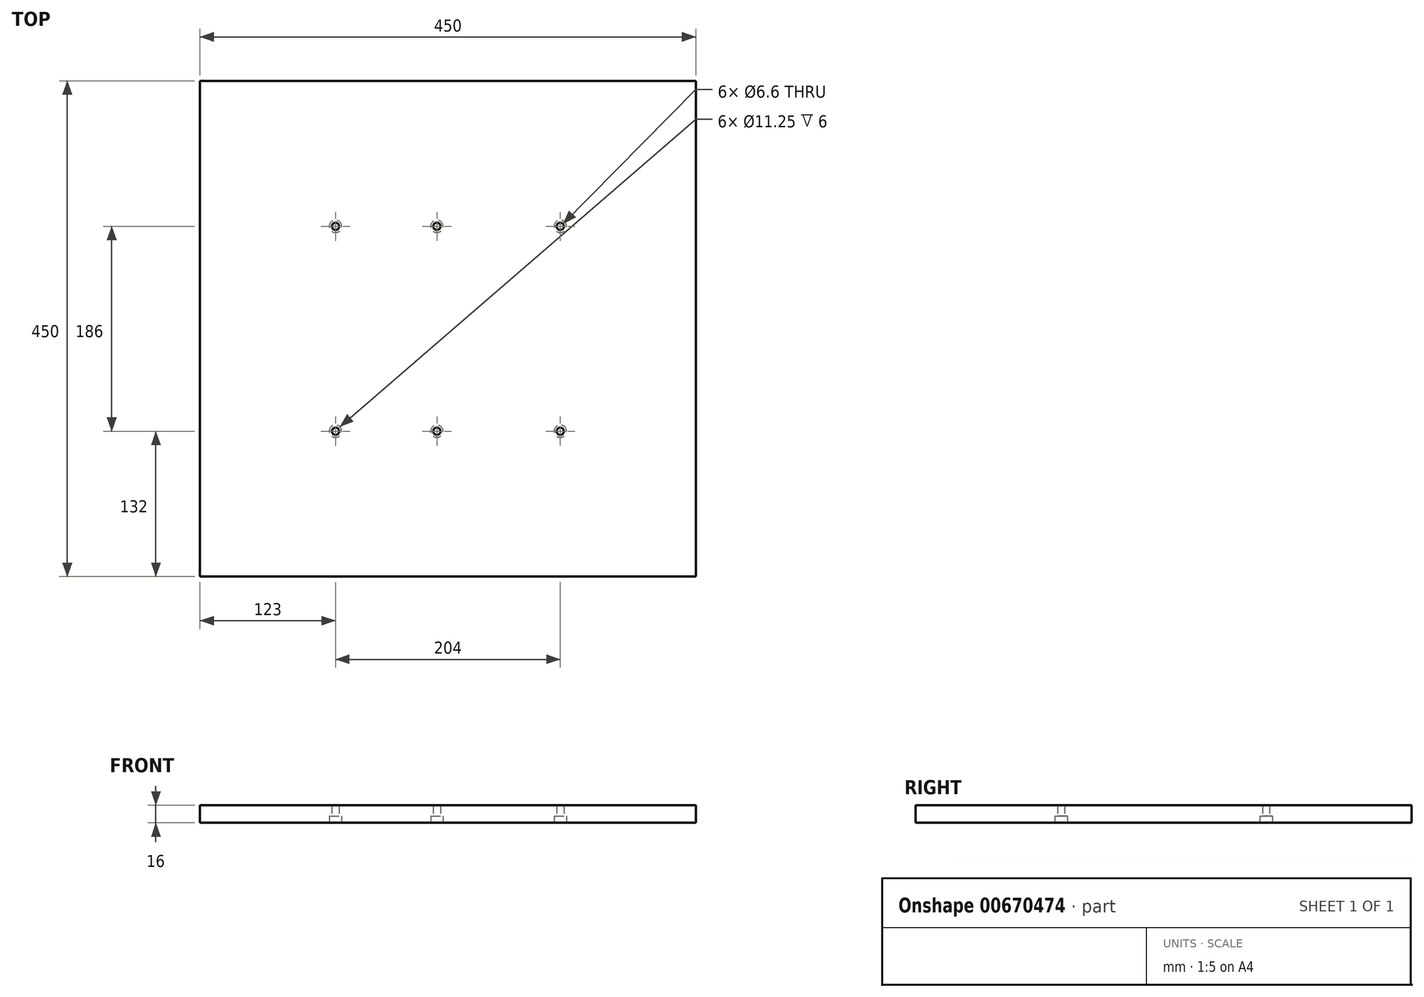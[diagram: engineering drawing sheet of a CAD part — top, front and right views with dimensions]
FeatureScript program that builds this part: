
annotation { "Feature Type Name" : "Feature", "Feature Type Description" : "" }
export const myFeature = defineFeature(function(context is Context, id is Id, definition is map)
    precondition{}
    {
        {
            var Q0;
            Q0=qCreatedBy(makeId("Top.planeOp"),FACE);
            var sketch = newSketch(context, id + "F0", { "sketchPlane" : qUnion([Q0])});
            skLineSegment(sketch, "E0.bottom", {"start": v(225, -225) * mm, "end": v(-225, -225) * mm});
            skLineSegment(sketch, "E0.top", {"start": v(225, 225) * mm, "end": v(-225, 225) * mm});
            skLineSegment(sketch, "E0.left", {"start": v(225, -225) * mm, "end": v(225, 225) * mm});
            skLineSegment(sketch, "E0.right", {"start": v(-225, -225) * mm, "end": v(-225, 225) * mm});
            skPoint(sketch, "E0.middle", {"position": v(0, 0) * mm});
            skSolve(sketch);
        }
        {
            var Q0;
            Q0 = qSketchRegion(id + "F0", true);
            extrude(context, id + "F1", {"entities" : qUnion([Q0]), "depth" : 16 * mm, "offsetDistance" : 25.4 * mm});
        }
        {
            var Q0;
            Q0=qCreatedBy(makeId("Top.planeOp"),FACE);
            var sketch = newSketch(context, id + "F2", { "sketchPlane" : qUnion([Q0])});
            skCircle(sketch, "E1", {"center": v(-102, -93) * mm, "radius": 3.3 * mm});
            skCircle(sketch, "E2", {"center": v(-10, -93) * mm, "radius": 3.3 * mm});
            skCircle(sketch, "E3", {"center": v(102, -93) * mm, "radius": 3.3 * mm});
            skCircle(sketch, "E4", {"center": v(-10, 93) * mm, "radius": 3.3 * mm});
            skCircle(sketch, "E5", {"center": v(102, 93) * mm, "radius": 3.3 * mm});
            skCircle(sketch, "E6", {"center": v(-102, 93) * mm, "radius": 3.3 * mm});
            skLineSegment(sketch, "E7.bottom", {"start": v(-102, 93) * mm, "end": v(102, 93) * mm, "construction": true});
            skLineSegment(sketch, "E7.top", {"start": v(-102, -93) * mm, "end": v(102, -93) * mm, "construction": true});
            skLineSegment(sketch, "E7.left", {"start": v(-102, 93) * mm, "end": v(-102, -93) * mm, "construction": true});
            skLineSegment(sketch, "E7.right", {"start": v(102, 93) * mm, "end": v(102, -93) * mm, "construction": true});
            skLineSegment(sketch, "E8", {"start": v(-102, -93) * mm, "end": v(102, 93) * mm, "construction": true});
            skLineSegment(sketch, "E9", {"start": v(-102, 93) * mm, "end": v(102, -93) * mm, "construction": true});
            skPoint(sketch, "E10", {"position": v(0, 0) * mm});
            skSolve(sketch);
        }
        {
            var Q0;
            Q0=sQuery(id+"F2.wireOp",VERTEX,"E7.left.start");
            var Q1;
            Q1=sQuery(id+"F2.wireOp",VERTEX,"E7.left.end");
            var Q2;
            Q2=sQuery(id+"F2.wireOp",VERTEX,"E2.center");
            var Q3;
            Q3=sQuery(id+"F2.wireOp",VERTEX,"E4.center");
            var Q4;
            Q4=sQuery(id+"F2.wireOp",VERTEX,"E7.right.start");
            var Q5;
            Q5=sQuery(id+"F2.wireOp",VERTEX,"E7.top.end");
            var Q6;
            Q6=makeQuery(id+"F1.opExtrude","SWEPT_BODY",BODY,{"disambiguationData":[OSD([sQuery(id+"F0.wireOp",EDGE,"E0.bottom"),sQuery(id+"F0.wireOp",EDGE,"E0.top"),sQuery(id+"F0.wireOp",EDGE,"E0.left"),sQuery(id+"F0.wireOp",EDGE,"E0.right")])]});
            hole(context, id + "F3", {"style" : HoleStyle.C_BORE, "endStyle" : HoleEndStyle.THROUGH, "oppositeDirection" : true, "standardTappedOrClearance" : lookupTablePath({ "standard" : "ISO", "fit" : "Normal", "size" : "M6", "type" : "Clearance" }), "standardBlindInLast" : lookupTablePath({ "fit" : "Standard", "standard" : "ISO", "size" : "M6", "type" : "Clearance" }), "holeDiameter" : 6.6 * mm, "cBoreDiameter" : 11.25 * mm, "cBoreDepth" : 6 * mm, "majorDiameter" : 5 * mm, "isTappedThrough" : true, "tappedDepth" : 12 * mm, "tapClearance" : 3, "locations" : qUnion([Q0, Q1, Q2, Q3, Q4, Q5]), "scope" : qUnion([Q6])});
        }
    });
